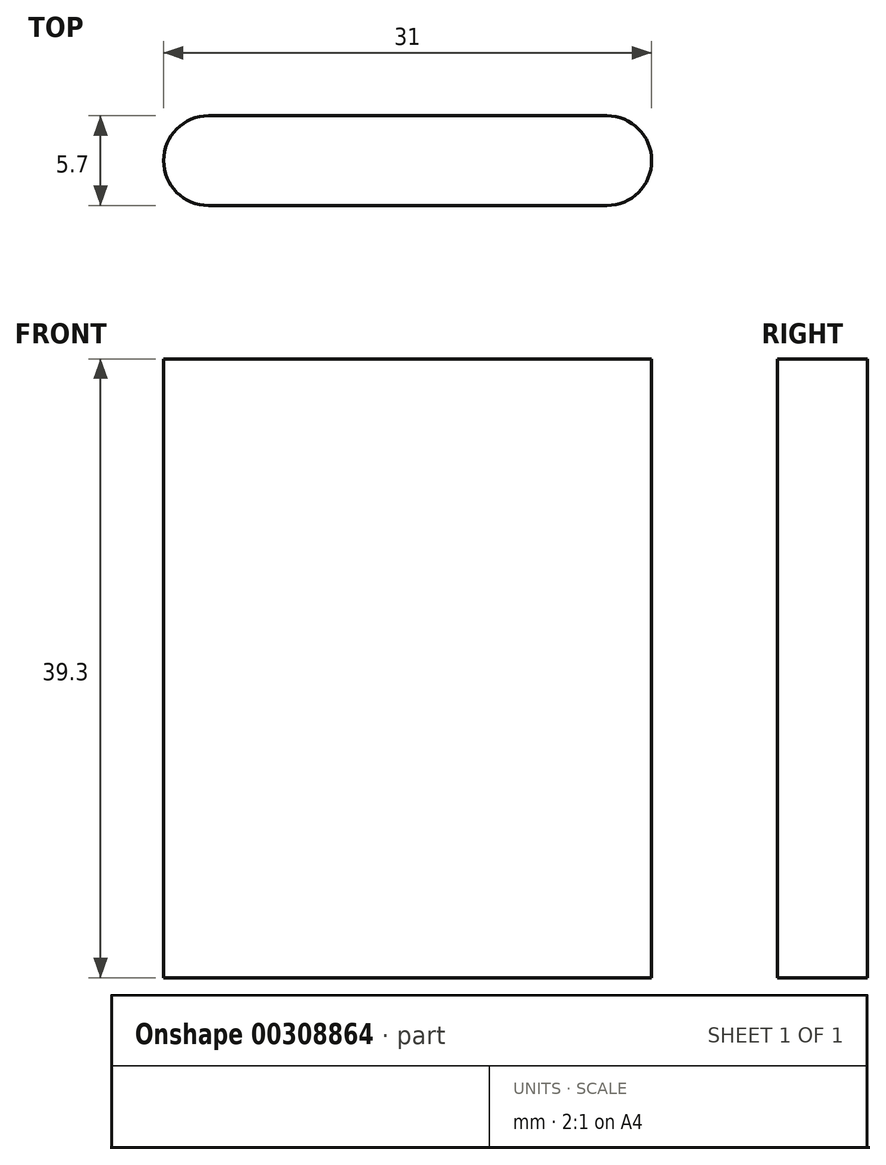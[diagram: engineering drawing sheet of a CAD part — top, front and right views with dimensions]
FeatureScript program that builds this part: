
annotation { "Feature Type Name" : "Feature", "Feature Type Description" : "" }
export const myFeature = defineFeature(function(context is Context, id is Id, definition is map)
    precondition{}
    {
        {
            var Q0;
            Q0=qCreatedBy(makeId("Top.planeOp"),FACE);
            var sketch = newSketch(context, id + "F0", { "sketchPlane" : qUnion([Q0])});
            skArc(sketch, "E0", {"start": v(25.3, -2.85) * mm, "mid": v(28.15, 0) * mm, "end": v(25.3, 2.85) * mm});
            skArc(sketch, "E1", {"start": v(0, 2.85) * mm, "mid": v(-2.85, 0) * mm, "end": v(0, -2.85) * mm});
            skLineSegment(sketch, "E2", {"start": v(0, 2.85) * mm, "end": v(25.3, 2.85) * mm});
            skLineSegment(sketch, "E3", {"start": v(25.3, -2.85) * mm, "end": v(0, -2.85) * mm});
            skSolve(sketch);
        }
        {
            var Q0;
            Q0=makeQuery(id+"F0.imprint","IMPRINT",FACE,{"disambiguationData":[TD([[makeQuery(id+"F0.imprint","IMPRINT",EDGE,{"derivedFrom":sQuery(id+"F0.wireOp",EDGE,"E0")}),1.0]])]});
            extrude(context, id + "F1", {"entities" : qUnion([Q0]), "depth" : 39.3 * mm});
        }
    });
